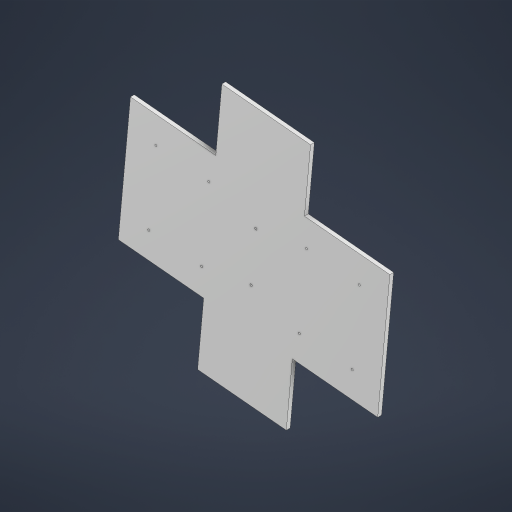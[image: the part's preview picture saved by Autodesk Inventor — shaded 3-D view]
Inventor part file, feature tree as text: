
AUTODESK INVENTOR PART (.ipt)
format: ipt  version: 2024.2 (Build 282272000, 272)  size: 308,736 bytes
history: native  units: in
note: dims shown in document units (in); Inventor stores cm internally (conversion verified against a paired STEP export)
features: reference x18, other x10, sketch x1, plane x1, extrude x1
ambient origin geometry x8: Origin, YZ Plane, XZ Plane, XY Plane, X Axis, Y Axis, Z Axis, Center Point
bodies: Solid1 (feature_tree)
feature tree (31):
  sketch  "Sketch1"  dims[d0=0.126in d1=0.126in d2=0.126in d3=0.126in d4=0.126in d5=0.126in d6=0.126in d7=0.126in d8=0.144in d9=0.144in d10=1.0in d11=0.0in]
  plane  "Work Plane1"
  extrude  "Extrusion1"  Depth=0.126in
  reference  "Reference1"
  reference  "Reference2"
  reference  "Reference3"
  reference  "Reference4"
  reference  "Reference5"
  reference  "Reference6"
  reference  "Reference7"
  reference  "Reference8"
  reference  "Reference9"
  reference  "Reference10"
  reference  "Reference11"
  reference  "Reference12"
  reference  "Reference13"
  reference  "Reference14"
  reference  "Reference15"
  reference  "Reference16"
  reference  "Reference17"
  reference  "Reference18"
  other  "Assembly1"
  other  "Pod_pre_mirror:1"
  other  "Pod_pre_mirror_Top_Right:1"
  other  "Pod_pre_mirror_Bottom_Left:1"
  other  "Pod:1"
  other  "Lower_Plate:1"
  other  "REV Robotics Expansion Hub REV-31-1153 - Expansion Hub:1"
  other  "Servo Power Module REV-11-1144 - Servo Power Module REV-11-1144:1"
  other  "top_shell"
  other  "Control Hub REV-31-1152 - Control Hub REV-31-1152:1"
